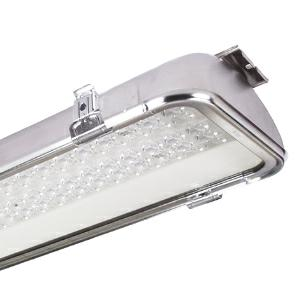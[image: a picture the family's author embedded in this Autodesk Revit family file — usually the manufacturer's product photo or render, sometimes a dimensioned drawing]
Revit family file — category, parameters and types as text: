
# Revit family: 3f_filippi_-_beta_235_93_vt_ampio_3f_filippi_-_52832_-_beta_235_led_932x50_dali_ampio_vt_l1565
name_source: partatom
category: Lighting Fixtures
units: mm (PartAtom-declared; Revit-internal decimal feet)

## family parameters
Cut with Voids When Loaded = No
Host = Face
Light Source = No
Part Type = Normal
Room Calculation Point = No
Round Connector Dimension = Use Diameter
Shared = No

## types (1)
- 3F Filippi - Beta 235 93 VT Ampio (1 x LED, 15581 lm, 99 W, 4000 K)
    Apparent Load = 99 VA
    Approval mark = CE
    CIE Flux Codes = 55 92 99 100 100
    Color Rendering = 80
    Color Temperature = 4000 K
    Control Gear = Electronic transformer
    Default Elevation = 1800 mm
    Description = ILLUMINOTECHNICAL
Luminous efficiency 100% (DLOR 100%, ULOR 0%).
Initial luminous flux of the luminaire 15581 lm.
Wide symmetric distribution.
Installation Interdistance Transv.D = 1.18 x hu - Long.D = 1.19 x hu.
Tabular UGR (CIE 117 - 4H-8H; S=0.25H; 70/50/20): RUG 21.7 - 23.4.
Beam angle: 100° - 106°.
Luminous efficacy 157 lm/W.
Lifetime (L93/B10): 30000 h. (tq+25°C)
Lifetime (L90/B10): 50000 h. (tq+25°C)
Lifetime (L85/B10): 80000 h. (tq+25°C)
Lifetime (L80/B10): 100000 h. (tq+25°C)
Lifetime (L85/B10): 50000 h. (tq+45°C)
Sudden decreased luminous flux after 50000 hours: 0% (C0).
Photobiological safety in compliance with IEC/TR 62778: RG0 risk exempt, (IEC 62471).
In compliance with IEC/EN 62722-2-1 - IEC/EN 62717 standards.

SOURCE
2 linear LED modules 50W/840.
Energy efficiency class (UE 2019/2020 - UE 2019/2015): C.
CIE 13.3 Colour rendering index: CRI >80 (R9 <50%).
IES TM-30 Fidelity Index: Rf = 84 Rg = 95.
CCT nominal colour temperature 4000 K.
Colour initial tolerance (MacAdam): SDCM 3.

MECHANICAL
Housing in AISI 304 stainless steel, pressed in one single piece.
VT transparent glass, non-combustible, single-piece perimeter frame in stainless steel.
Oversized gear-tray reflector unit in highly reflective white painted hot-galvanised steel.
Methacrylate (PMMA) lenses with external flat surface.
Stainless steel snap-lock clips for diffuser mounting (safety n° 4 per fixture).
Luminaire with limited surface temperature. - D - (EN 60598-2-24)
Dimensions: 1565x235 mm, height 105 mm. Weight 11.44 kg.
IP65 protection degree.
Mechanical strength to impacts IK09 (10 joule).
Glow-wire test resistance 960°C.

ELECTRICAL
Halogen Free DALI-2 DATI (Parts 251, 252, 253), PUSH-DIM, electronic wiring 230V-50/60Hz, power factor 0.95 at full load, THD <25%, constant output current, class I, 1 driver, 1 DALI addresse.
Power of the luminaire 99 W.
ENEC - CE.
Flicker: <4%.
Luminaire compliant with EN 60598-2-22 for power supply from a centralised emergency system CPSS (Central Power Supply System), not incorporated in the luminaire - high risk areas excluded. The default power and flux are 100% in AC and 15% in DC.
Ambient temperature from -20°C to +45°C.
Temperature class T6 max 85°C.
Quick connection via M25 5P connector with 9-13 mm tightening range.
Relative humidity UR: <85%.

INSTALLATION
Ceiling / Suspended / Wall.
All accessories dedicated to this product are available on the Catalog and on our website www.3F-Filippi.com.

APPLICATIONS
Dry, dusty indoor environments, subject to occasional water splashes.
Any environments except the ones where the luminaire materials are unsuitable.
Industrial environments, warehouses, environments where security locks are required on all clips, e.g. prisons (on request).
Environments in which it is necessary a total protection against falling fragments (eg environments with foodstuffs or machines with moving parts or with extreme temperature changes), use luminaires with laminated glass.
Tempered glass is not immune to falling fragments from harmless and caused by shocks or exceptionally derived from the tempering process.

LIGHT MANAGEMENT
Recommended minimum setting: 10%.
The luminaire, equipped with (DALI-2 DATI) driver, can be controlled manually with 3F Easy Dim technology or automatically/manually with wired or wireless DALI/D2D control systems.
The D2D driver guarantees interoperability with other devices with the same certification by making the following information available:
Device Data (Part 251), Energy Report (Part 252), Diagnosis & Maintenance (Part 253).
In electrical systems without a regulation system (manual or automatic) and DALI bus, a suitable jumper must be made on the DA-DA terminals of the appliance.

WARNING
Fixture not suitable for cold stores with an ambient temperature <0°C and/or relative humidity >85%.
Luminaire designed for disposal/recycling at end-of-life.
Replaceable (LED only) light source by a professional. Replaceable control gear by a professional.
    Height = 105 mm
    Lamp = 1 x LED
    Lamp Light Flux = 15581 lm
    Lamp Power = 99 W
    Lamp count = 1
    Length = 1565 mm
    Lifetime = 50000 h
    Luminous efficacy = 157 lm/W
    Manufacturer = 3F Filippi
    ModVariant = No
    Model = 3F Filippi - 52832 - Beta 235 LED 932x50 DALI AMPIO VT L1565
    Mounting Place = Ceiling
    Mounting Type = Pendant
    Number of Poles = 1
    OnlyDefault = Yes
    Power Factor = 1
    Product Name = 3F Filippi - Beta 235 93 VT Ampio
    Product group = pendant luminaire
    ProductGroupID = 9
    Protection Class = Protection class I
    Protection Degree = IP 65
    RLX_Detail_Level = 1
    RLX_Emergency_Light_Flux = 0 lm
    RLX_Emergency_Type = 0
    RLX_Emergency_Type_DB = No
    RlxData = <blob elided: 91581 chars, md5=1c0e288a>
    Socket = socket
    Standby Power = 0 W
    System Light Flux = 15581 lm
    System Power = 99 W
    Type Comments = Product without accessories
    Type Image = 3ffilippi_52832.jpg
    URL = http://relux.com
    VarID = ---
    Voltage = 0 V
    Weight = 0.00 kg
    Width = 235 mm

## geometry (parser evidence)
native form markers: Blend x4, Sweep x11
no freeform markers — native parametric forms only
